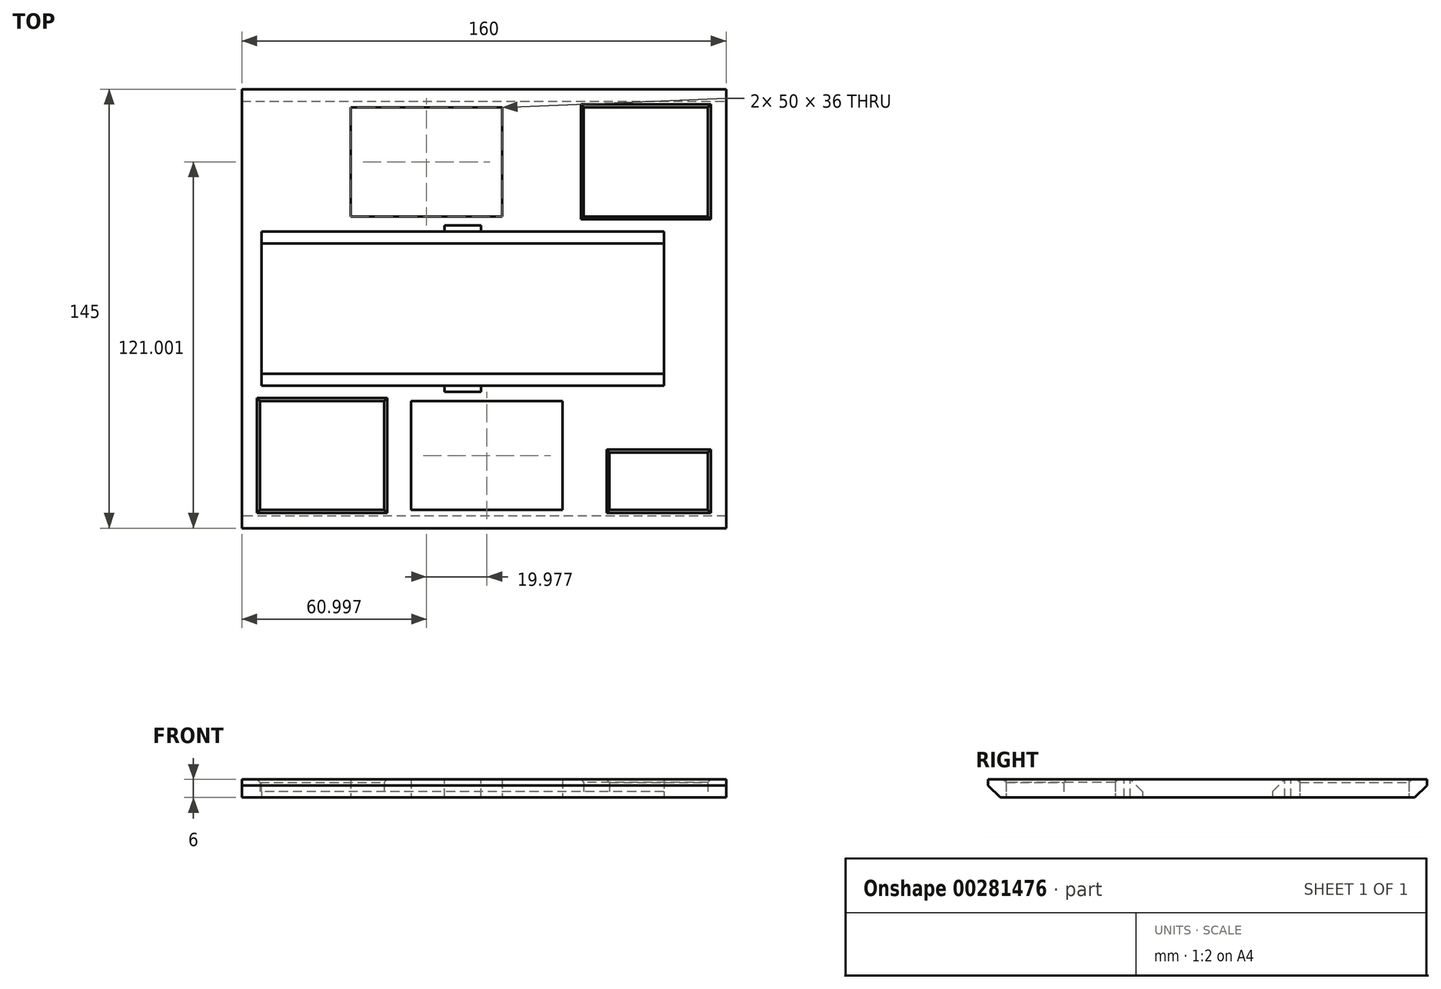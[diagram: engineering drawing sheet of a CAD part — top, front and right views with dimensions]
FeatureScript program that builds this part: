
annotation { "Feature Type Name" : "Feature", "Feature Type Description" : "" }
export const myFeature = defineFeature(function(context is Context, id is Id, definition is map)
    precondition{}
    {
        {
            var Q0;
            Q0=qCreatedBy(makeId("Top.planeOp"),FACE);
            var sketch = newSketch(context, id + "F0", { "sketchPlane" : qUnion([Q0])});
            skLineSegment(sketch, "E0.bottom", {"start": v(-86.04, 79.75) * mm, "end": v(73.96, 79.75) * mm});
            skLineSegment(sketch, "E0.top", {"start": v(-86.04, -65.25) * mm, "end": v(73.96, -65.25) * mm});
            skLineSegment(sketch, "E0.left", {"start": v(-86.04, 79.75) * mm, "end": v(-86.04, -65.25) * mm});
            skLineSegment(sketch, "E0.right", {"start": v(73.96, 79.75) * mm, "end": v(73.96, -65.25) * mm});
            skLineSegment(sketch, "E1.bottom", {"start": v(67.96, 73.75) * mm, "end": v(26.96, 73.75) * mm});
            skLineSegment(sketch, "E1.top", {"start": v(67.96, 37.75) * mm, "end": v(26.96, 37.75) * mm});
            skLineSegment(sketch, "E1.left", {"start": v(67.96, 73.75) * mm, "end": v(67.96, 37.75) * mm});
            skLineSegment(sketch, "E1.right", {"start": v(26.96, 73.75) * mm, "end": v(26.96, 37.75) * mm});
            skLineSegment(sketch, "E2.bottom", {"start": v(-80.04, -59.25) * mm, "end": v(-39.04, -59.25) * mm});
            skLineSegment(sketch, "E2.top", {"start": v(-80.04, -23.25) * mm, "end": v(-39.04, -23.25) * mm});
            skLineSegment(sketch, "E2.left", {"start": v(-80.04, -59.25) * mm, "end": v(-80.04, -23.25) * mm});
            skLineSegment(sketch, "E2.right", {"start": v(-39.04, -59.25) * mm, "end": v(-39.04, -23.25) * mm});
            skLineSegment(sketch, "E3.bottom", {"start": v(67.96, -59.25) * mm, "end": v(35.46, -59.25) * mm});
            skLineSegment(sketch, "E3.top", {"start": v(67.96, -40.25) * mm, "end": v(35.46, -40.25) * mm});
            skLineSegment(sketch, "E3.left", {"start": v(67.96, -59.25) * mm, "end": v(67.96, -40.25) * mm});
            skLineSegment(sketch, "E3.right", {"start": v(35.46, -59.25) * mm, "end": v(35.46, -40.25) * mm});
            skLineSegment(sketch, "E4.bottom", {"start": v(-79.56, 28.75) * mm, "end": v(53.44, 28.75) * mm});
            skLineSegment(sketch, "E4.top", {"start": v(-79.56, -14.25) * mm, "end": v(53.44, -14.25) * mm});
            skLineSegment(sketch, "E4.left", {"start": v(-79.56, 28.75) * mm, "end": v(-79.56, -14.25) * mm});
            skLineSegment(sketch, "E4.right", {"start": v(53.44, 28.75) * mm, "end": v(53.44, -14.25) * mm});
            skLineSegment(sketch, "E5.bottom", {"start": v(-50.04, 73.75) * mm, "end": v(-0.04, 73.75) * mm});
            skLineSegment(sketch, "E5.top", {"start": v(-50.04, 37.75) * mm, "end": v(-0.04, 37.75) * mm});
            skLineSegment(sketch, "E5.left", {"start": v(-50.04, 73.75) * mm, "end": v(-50.04, 37.75) * mm});
            skLineSegment(sketch, "E5.right", {"start": v(-0.04, 73.75) * mm, "end": v(-0.04, 37.75) * mm});
            skLineSegment(sketch, "E6.bottom", {"start": v(-30.07, -59.25) * mm, "end": v(19.93, -59.25) * mm});
            skLineSegment(sketch, "E6.top", {"start": v(-30.07, -23.25) * mm, "end": v(19.93, -23.25) * mm});
            skLineSegment(sketch, "E6.left", {"start": v(-30.07, -59.25) * mm, "end": v(-30.07, -23.25) * mm});
            skLineSegment(sketch, "E6.right", {"start": v(19.93, -59.25) * mm, "end": v(19.93, -23.25) * mm});
            skSolve(sketch);
        }
        {
            var Q0;
            Q0=makeQuery(id+"F0.imprint","IMPRINT",FACE,{"disambiguationData":[TD([[makeQuery(id+"F0.imprint","IMPRINT",EDGE,{"derivedFrom":sQuery(id+"F0.wireOp",EDGE,"E0.bottom")}),-1.0]])]});
            extrude(context, id + "F1", {"entities" : qUnion([Q0]), "depth" : 6 * mm});
        }
        {
            var Q0;
            Q0=makeQuery(id+"F1.opExtrude","CAP_EDGE",EDGE,{"disambiguationData":[OSD([sQuery(id+"F0.wireOp",EDGE,"E0.top")])],"isStart":true});
            var Q1;
            Q1=makeQuery(id+"F1.opExtrude","CAP_EDGE",EDGE,{"disambiguationData":[OSD([sQuery(id+"F0.wireOp",EDGE,"E0.bottom")])],"isStart":true});
            var Q2;
            Q2=makeQuery(id+"F1.opExtrude","CAP_EDGE",EDGE,{"disambiguationData":[OSD([sQuery(id+"F0.wireOp",EDGE,"E4.bottom")])],"isStart":false});
            var Q3;
            Q3=makeQuery(id+"F1.opExtrude","CAP_EDGE",EDGE,{"disambiguationData":[OSD([sQuery(id+"F0.wireOp",EDGE,"E4.top")])],"isStart":false});
            chamfer(context, id + "F2", {"entities" : qUnion([Q0, Q1, Q2, Q3]), "width" : 4 * mm, "tangentPropagation" : true});
        }
        {
            var Q0;
            Q0=makeQuery(id+"F1.opExtrude","CAP_FACE",FACE,{"disambiguationData":[OSD([sQuery(id+"F0.wireOp",EDGE,"E0.bottom"),sQuery(id+"F0.wireOp",EDGE,"E0.top"),sQuery(id+"F0.wireOp",EDGE,"E0.left"),sQuery(id+"F0.wireOp",EDGE,"E0.right"),sQuery(id+"F0.wireOp",EDGE,"E1.bottom"),sQuery(id+"F0.wireOp",EDGE,"E1.top"),sQuery(id+"F0.wireOp",EDGE,"E1.left"),sQuery(id+"F0.wireOp",EDGE,"E1.right"),sQuery(id+"F0.wireOp",EDGE,"E2.bottom"),sQuery(id+"F0.wireOp",EDGE,"E2.top"),sQuery(id+"F0.wireOp",EDGE,"E2.left"),sQuery(id+"F0.wireOp",EDGE,"E2.right"),sQuery(id+"F0.wireOp",EDGE,"E3.bottom"),sQuery(id+"F0.wireOp",EDGE,"E3.top"),sQuery(id+"F0.wireOp",EDGE,"E3.left"),sQuery(id+"F0.wireOp",EDGE,"E3.right"),sQuery(id+"F0.wireOp",EDGE,"E4.bottom"),sQuery(id+"F0.wireOp",EDGE,"E4.top"),sQuery(id+"F0.wireOp",EDGE,"E4.left"),sQuery(id+"F0.wireOp",EDGE,"E4.right"),sQuery(id+"F0.wireOp",EDGE,"E5.bottom"),sQuery(id+"F0.wireOp",EDGE,"E5.top"),sQuery(id+"F0.wireOp",EDGE,"E5.left"),sQuery(id+"F0.wireOp",EDGE,"E5.right"),sQuery(id+"F0.wireOp",EDGE,"E6.bottom"),sQuery(id+"F0.wireOp",EDGE,"E6.top"),sQuery(id+"F0.wireOp",EDGE,"E6.left"),sQuery(id+"F0.wireOp",EDGE,"E6.right")])],"isStart":false});
            var sketch = newSketch(context, id + "F3", { "sketchPlane" : qUnion([Q0])});
            skLineSegment(sketch, "E7", {"start": v(67.96, 73.75) * mm, "end": v(26.96, 37.75) * mm, "construction": true});
            skLineSegment(sketch, "E8", {"start": v(26.96, 73.75) * mm, "end": v(67.96, 37.75) * mm, "construction": true});
            skLineSegment(sketch, "E9", {"start": v(35.46, -40.25) * mm, "end": v(67.96, -59.25) * mm, "construction": true});
            skLineSegment(sketch, "E10", {"start": v(67.96, -40.25) * mm, "end": v(35.46, -59.25) * mm, "construction": true});
            skLineSegment(sketch, "E11", {"start": v(-39.04, -23.25) * mm, "end": v(-80.04, -59.25) * mm, "construction": true});
            skLineSegment(sketch, "E12", {"start": v(-80.04, -23.25) * mm, "end": v(-39.04, -59.25) * mm, "construction": true});
            skPoint(sketch, "E13", {"position": v(47.46, 55.75) * mm});
            skPoint(sketch, "E14", {"position": v(51.7, -49.75) * mm});
            skPoint(sketch, "E15", {"position": v(-59.54, -41.25) * mm});
            skLineSegment(sketch, "E16", {"start": v(-79.56, 32.75) * mm, "end": v(53.44, -18.25) * mm, "construction": true});
            skLineSegment(sketch, "E17", {"start": v(53.44, 32.75) * mm, "end": v(-79.56, -18.25) * mm, "construction": true});
            skPoint(sketch, "E18", {"position": v(-13.06, 7.25) * mm});
            skLineSegment(sketch, "E19", {"start": v(-13.06, 7.25) * mm, "end": v(-13.06, 37.75) * mm, "construction": true});
            skLineSegment(sketch, "E20", {"start": v(-13.06, 7.25) * mm, "end": v(-13.06, -23.25) * mm, "construction": true});
            skPoint(sketch, "E20.endSnap0", {"position": v(-13.06, -18.25) * mm});
            skLineSegment(sketch, "E21", {"start": v(47.46, 55.75) * mm, "end": v(47.46, 79.75) * mm, "construction": true});
            skLineSegment(sketch, "E22", {"start": v(47.46, 55.75) * mm, "end": v(47.46, 32.75) * mm, "construction": true});
            skLineSegment(sketch, "E23", {"start": v(-59.54, -41.25) * mm, "end": v(-59.54, -18.25) * mm, "construction": true});
            skLineSegment(sketch, "E24", {"start": v(-59.54, -41.25) * mm, "end": v(-59.54, -65.25) * mm, "construction": true});
            skLineSegment(sketch, "E25", {"start": v(51.7, -49.75) * mm, "end": v(51.7, -30.34) * mm, "construction": true});
            skPoint(sketch, "E26", {"position": v(-13.06, 33.75) * mm});
            skPoint(sketch, "E27", {"position": v(-13.06, -19.25) * mm});
            skLineSegment(sketch, "E28.bottom", {"start": v(-7.06, 32.75) * mm, "end": v(-19.06, 32.75) * mm});
            skLineSegment(sketch, "E28.top", {"start": v(-7.06, 34.75) * mm, "end": v(-19.06, 34.75) * mm});
            skLineSegment(sketch, "E28.left", {"start": v(-7.06, 32.75) * mm, "end": v(-7.06, 34.75) * mm});
            skLineSegment(sketch, "E28.right", {"start": v(-19.06, 32.75) * mm, "end": v(-19.06, 34.75) * mm});
            skLineSegment(sketch, "E29.bottom", {"start": v(-7.06, -18.25) * mm, "end": v(-19.06, -18.25) * mm});
            skLineSegment(sketch, "E29.top", {"start": v(-7.06, -20.25) * mm, "end": v(-19.06, -20.25) * mm});
            skLineSegment(sketch, "E29.left", {"start": v(-7.06, -18.25) * mm, "end": v(-7.06, -20.25) * mm});
            skLineSegment(sketch, "E29.right", {"start": v(-19.06, -18.25) * mm, "end": v(-19.06, -20.25) * mm});
            skLineSegment(sketch, "E30", {"start": v(51.7, -49.75) * mm, "end": v(51.7, -65.25) * mm, "construction": true});
            skPoint(sketch, "E31", {"position": v(51.7, -35.82) * mm});
            skPoint(sketch, "E32", {"position": v(51.7, -62.1) * mm});
            skPoint(sketch, "E33", {"position": v(-106.61, 16.14) * mm});
            skPoint(sketch, "E34", {"position": v(-59.54, -20.67) * mm});
            skPoint(sketch, "E35", {"position": v(-59.54, -62.1) * mm});
            skPoint(sketch, "E36", {"position": v(47.46, 76.12) * mm});
            skPoint(sketch, "E37", {"position": v(47.46, 35.15) * mm});
            skSolve(sketch);
        }
        {
            var Q0;
            Q0=makeQuery(id+"F3.imprint","IMPRINT",FACE,{"disambiguationData":[TD([[makeQuery(id+"F3.imprint","IMPRINT",EDGE,{"derivedFrom":sQuery(id+"F3.wireOp",EDGE,"E28.bottom")}),1.0]])]});
            var Q1;
            Q1=makeQuery(id+"F3.imprint","IMPRINT",FACE,{"disambiguationData":[TD([[makeQuery(id+"F3.imprint","IMPRINT",EDGE,{"derivedFrom":sQuery(id+"F3.wireOp",EDGE,"E29.bottom")}),1.0]])]});
            extrude(context, id + "F4", {"entities" : qUnion([Q0, Q1]), "operationType" : NewBodyOperationType.REMOVE, "endBound" : BoundingType.THROUGH_ALL, "oppositeDirection" : true, "depth" : 25 * mm});
        }
        {
            var Q0;
            Q0=makeQuery(id+"F1.opExtrude","CAP_EDGE",EDGE,{"disambiguationData":[OSD([sQuery(id+"F0.wireOp",EDGE,"E1.bottom")])],"isStart":false});
            var Q1;
            Q1=makeQuery(id+"F1.opExtrude","CAP_EDGE",EDGE,{"disambiguationData":[OSD([sQuery(id+"F0.wireOp",EDGE,"E1.right")])],"isStart":false});
            var Q2;
            Q2=makeQuery(id+"F1.opExtrude","CAP_EDGE",EDGE,{"disambiguationData":[OSD([sQuery(id+"F0.wireOp",EDGE,"E1.left")])],"isStart":false});
            var Q3;
            Q3=makeQuery(id+"F1.opExtrude","CAP_EDGE",EDGE,{"disambiguationData":[OSD([sQuery(id+"F0.wireOp",EDGE,"E1.top")])],"isStart":false});
            var Q4;
            Q4=makeQuery(id+"F1.opExtrude","CAP_EDGE",EDGE,{"disambiguationData":[OSD([sQuery(id+"F0.wireOp",EDGE,"E3.top")])],"isStart":false});
            var Q5;
            Q5=makeQuery(id+"F1.opExtrude","CAP_EDGE",EDGE,{"disambiguationData":[OSD([sQuery(id+"F0.wireOp",EDGE,"E3.left")])],"isStart":false});
            var Q6;
            Q6=makeQuery(id+"F1.opExtrude","CAP_EDGE",EDGE,{"disambiguationData":[OSD([sQuery(id+"F0.wireOp",EDGE,"E3.bottom")])],"isStart":false});
            var Q7;
            Q7=makeQuery(id+"F1.opExtrude","CAP_EDGE",EDGE,{"disambiguationData":[OSD([sQuery(id+"F0.wireOp",EDGE,"E3.right")])],"isStart":false});
            var Q8;
            Q8=makeQuery(id+"F1.opExtrude","CAP_EDGE",EDGE,{"disambiguationData":[OSD([sQuery(id+"F0.wireOp",EDGE,"E2.top")])],"isStart":false});
            var Q9;
            Q9=makeQuery(id+"F1.opExtrude","CAP_EDGE",EDGE,{"disambiguationData":[OSD([sQuery(id+"F0.wireOp",EDGE,"E2.bottom")])],"isStart":false});
            var Q10;
            Q10=makeQuery(id+"F1.opExtrude","CAP_EDGE",EDGE,{"disambiguationData":[OSD([sQuery(id+"F0.wireOp",EDGE,"E2.right")])],"isStart":false});
            var Q11;
            Q11=makeQuery(id+"F1.opExtrude","CAP_EDGE",EDGE,{"disambiguationData":[OSD([sQuery(id+"F0.wireOp",EDGE,"E2.left")])],"isStart":false});
            chamfer(context, id + "F5", {"entities" : qUnion([Q0, Q1, Q2, Q3, Q4, Q5, Q6, Q7, Q8, Q9, Q10, Q11]), "width" : 1 * mm, "tangentPropagation" : true});
        }
    });
